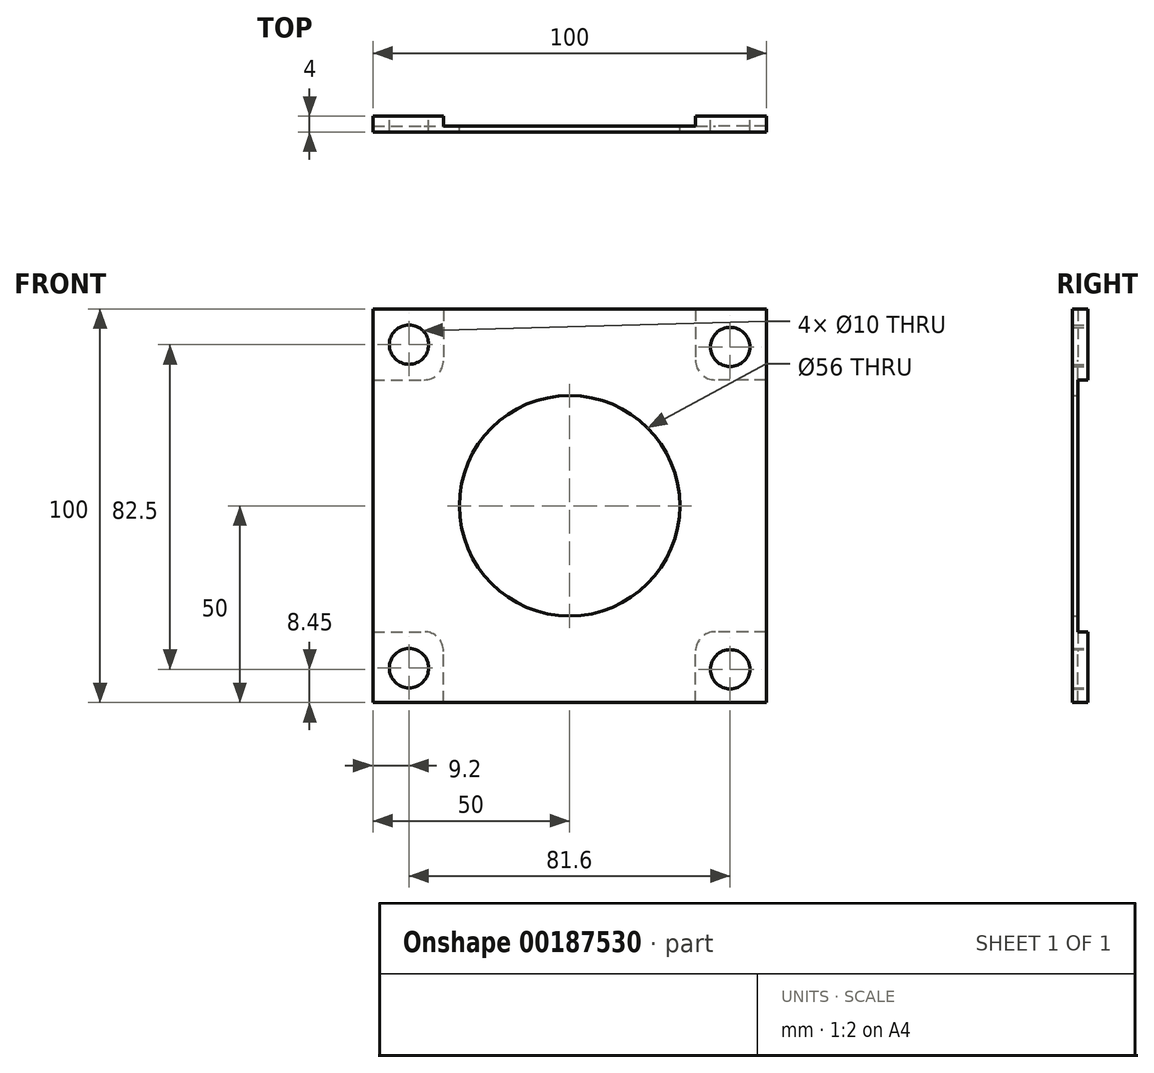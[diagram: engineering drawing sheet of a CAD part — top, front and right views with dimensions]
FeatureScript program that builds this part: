
annotation { "Feature Type Name" : "Feature", "Feature Type Description" : "" }
export const myFeature = defineFeature(function(context is Context, id is Id, definition is map)
    precondition{}
    {
        {
            var Q0;
            Q0=qCreatedBy(makeId("Front.planeOp"),FACE);
            var sketch = newSketch(context, id + "F0", { "sketchPlane" : qUnion([Q0])});
            skLineSegment(sketch, "E0.bottom", {"start": v(-50, 50) * mm, "end": v(50, 50) * mm});
            skLineSegment(sketch, "E0.top", {"start": v(-50, -50) * mm, "end": v(50, -50) * mm});
            skLineSegment(sketch, "E0.left", {"start": v(-50, 50) * mm, "end": v(-50, -50) * mm});
            skLineSegment(sketch, "E0.right", {"start": v(50, 50) * mm, "end": v(50, -50) * mm});
            skPoint(sketch, "E0.middle", {"position": v(0, 0) * mm});
            skCircle(sketch, "E1", {"center": v(0, 0) * mm, "radius": 28 * mm});
            skCircle(sketch, "E2", {"center": v(-40.8, 40.95) * mm, "radius": 5 * mm});
            skCircle(sketch, "E3", {"center": v(40.8, 40.35) * mm, "radius": 5 * mm});
            skCircle(sketch, "E4", {"center": v(40.8, -41.55) * mm, "radius": 5 * mm});
            skCircle(sketch, "E5", {"center": v(-40.8, -41.25) * mm, "radius": 5 * mm});
            skLineSegment(sketch, "E6.bottom", {"start": v(-50, 50) * mm, "end": v(-32, 50) * mm});
            skLineSegment(sketch, "E6.top", {"start": v(-50, 32) * mm, "end": v(-37, 32) * mm});
            skLineSegment(sketch, "E6.left", {"start": v(-50, 50) * mm, "end": v(-50, 32) * mm});
            skLineSegment(sketch, "E6.right", {"start": v(-32, 50) * mm, "end": v(-32, 37) * mm});
            skLineSegment(sketch, "E7.right", {"start": v(3881.68, -34.35) * mm, "end": v(3881.68, -34.05) * mm});
            skLineSegment(sketch, "E8.top", {"start": v(3881.68, -50) * mm, "end": v(3881.68, -50) * mm});
            skLineSegment(sketch, "E8.left", {"start": v(3881.68, -34.05) * mm, "end": v(3881.68, -50) * mm});
            skPoint(sketch, "E9.visualSharp", {"position": v(-32, 32) * mm});
            skArc(sketch, "E9.filletArc", {"start": v(-37, 32) * mm, "mid": v(-33.46, 33.46) * mm, "end": v(-32, 37) * mm});
            skLineSegment(sketch, "E10.bottom", {"start": v(50, 50) * mm, "end": v(32, 50) * mm});
            skLineSegment(sketch, "E10.top", {"start": v(50, 32) * mm, "end": v(37, 32) * mm});
            skLineSegment(sketch, "E10.left", {"start": v(50, 50) * mm, "end": v(50, 32) * mm});
            skLineSegment(sketch, "E10.right", {"start": v(32, 50) * mm, "end": v(32, 37) * mm});
            skPoint(sketch, "E11.visualSharp", {"position": v(32, 32) * mm});
            skArc(sketch, "E11.filletArc", {"start": v(32, 37) * mm, "mid": v(33.46, 33.46) * mm, "end": v(37, 32) * mm});
            skLineSegment(sketch, "E12.bottom", {"start": v(-50, -50) * mm, "end": v(-32, -50) * mm});
            skLineSegment(sketch, "E12.top", {"start": v(-50, -32) * mm, "end": v(-37, -32) * mm});
            skLineSegment(sketch, "E12.left", {"start": v(-50, -50) * mm, "end": v(-50, -32) * mm});
            skLineSegment(sketch, "E12.right", {"start": v(-32, -50) * mm, "end": v(-32, -37) * mm});
            skLineSegment(sketch, "E13.bottom", {"start": v(50, -50) * mm, "end": v(32, -50) * mm});
            skLineSegment(sketch, "E13.top", {"start": v(50, -32) * mm, "end": v(37, -32) * mm});
            skLineSegment(sketch, "E13.left", {"start": v(50, -50) * mm, "end": v(50, -32) * mm});
            skLineSegment(sketch, "E13.right", {"start": v(32, -50) * mm, "end": v(32, -37) * mm});
            skPoint(sketch, "E14.visualSharp", {"position": v(32, -32) * mm});
            skArc(sketch, "E14.filletArc", {"start": v(37, -32) * mm, "mid": v(33.46, -33.46) * mm, "end": v(32, -37) * mm});
            skPoint(sketch, "E15.visualSharp", {"position": v(-32, -32) * mm});
            skArc(sketch, "E15.filletArc", {"start": v(-32, -37) * mm, "mid": v(-33.46, -33.46) * mm, "end": v(-37, -32) * mm});
            skSolve(sketch);
        }
        {
            var Q0;
            Q0=makeQuery(id+"F0.imprint","IMPRINT",FACE,{"disambiguationData":[TD([[makeQuery(id+"F0.imprint","IMPRINT",EDGE,{"derivedFrom":sQuery(id+"F0.wireOp",EDGE,"E2")}),-1.0]])]});
            var Q1;
            Q1=makeQuery(id+"F0.imprint","IMPRINT",FACE,{"disambiguationData":[TD([[makeQuery(id+"F0.imprint","IMPRINT",EDGE,{"derivedFrom":sQuery(id+"F0.wireOp",EDGE,"E3")}),-1.0]])]});
            var Q2;
            Q2=makeQuery(id+"F0.imprint","IMPRINT",FACE,{"disambiguationData":[TD([[makeQuery(id+"F0.imprint","IMPRINT",EDGE,{"derivedFrom":sQuery(id+"F0.wireOp",EDGE,"E4")}),-1.0]])]});
            var Q3;
            Q3=makeQuery(id+"F0.imprint","IMPRINT",FACE,{"disambiguationData":[TD([[makeQuery(id+"F0.imprint","IMPRINT",EDGE,{"derivedFrom":sQuery(id+"F0.wireOp",EDGE,"E5")}),-1.0]])]});
            var Q4;
            Q4=makeQuery(id+"F0.imprint","IMPRINT",FACE,{"disambiguationData":[TD([[makeQuery(id+"F0.imprint","IMPRINT",EDGE,{"derivedFrom":sQuery(id+"F0.wireOp",EDGE,"E1")}),-1.0]])]});
            extrude(context, id + "F1", {"entities" : qUnion([Q0, Q1, Q2, Q3, Q4]), "depth" : 1.5 * mm});
        }
        {
            var Q0;
            Q0=makeQuery(id+"F0.imprint","IMPRINT",FACE,{"disambiguationData":[TD([[makeQuery(id+"F0.imprint","IMPRINT",EDGE,{"derivedFrom":sQuery(id+"F0.wireOp",EDGE,"E2")}),-1.0]])]});
            var Q1;
            Q1=makeQuery(id+"F0.imprint","IMPRINT",FACE,{"disambiguationData":[TD([[makeQuery(id+"F0.imprint","IMPRINT",EDGE,{"derivedFrom":sQuery(id+"F0.wireOp",EDGE,"E3")}),-1.0]])]});
            var Q2;
            Q2=makeQuery(id+"F0.imprint","IMPRINT",FACE,{"disambiguationData":[TD([[makeQuery(id+"F0.imprint","IMPRINT",EDGE,{"derivedFrom":sQuery(id+"F0.wireOp",EDGE,"E5")}),-1.0]])]});
            var Q3;
            Q3=makeQuery(id+"F0.imprint","IMPRINT",FACE,{"disambiguationData":[TD([[makeQuery(id+"F0.imprint","IMPRINT",EDGE,{"derivedFrom":sQuery(id+"F0.wireOp",EDGE,"E4")}),-1.0]])]});
            extrude(context, id + "F2", {"entities" : qUnion([Q0, Q1, Q2, Q3]), "operationType" : NewBodyOperationType.ADD, "oppositeDirection" : true, "depth" : 2.5 * mm});
        }
    });
